# Revit family: DAL_A3-TD06
name_source: partatom
category: Doors
revit_build: Autodesk Revit 2016 (Build: 20150220_1215(x64)
units: mm (PartAtom-declared; Revit-internal decimal feet)

## family parameters
Always vertical = Yes
Cut with Voids When Loaded = No
Host = Wall
Room Calculation Point = No
Shared = No

## types (1)
- TD06 1613 x 2032mm
    Construction Type = TD06
    Description = Purpose Made
    Door Frame = Purpose Made 1,2mm thick pressed metal steel frame with double rebate complete with lugs and base ties as supplied by manufacturer suitable for 115mm wall.
    Door Frame Finish = Red oxide primer factory finish as supplied by manufacturer. Prepare and paint one coat namelcoat zinc chromate metal primer. 1 coat merit universal undercoat and 2 coats gloss enamel paint colour as per finishing schedule.
    Door Panel = Purpose Made Semi-solid Medium Duty flush panel door leaf. 40mm thick with masonite veneer faces suitable for painting and edges to match veneer.
    Door Panel Finish = Stop with polyfilla spackle. Ensure that surfaces to be coated are clean, dry, firm and dust free. Apply 2-3 coats paint as specified.
    Frame Centre = 58 mm
    Function = Interior
    Height = 2064 mm  [stored 6.77165 ft]
    Manufacturer = Duro Pressings (Pty) Ltd.
    Note = All quantities & dimensions to be checked on site by contractor prior to ordering of any material, final quantities to be verified by architect. Schedules to be read in conjunction with latest floor layout drawings & finishing schedules.
    Other = Hinges as supplied by manufacturer. Manufacturer to take note of door weight and to supply hinges accordingly.
    Panel Height = 2032
    Panel Width = 1613
    Wall Closure = By host
    Width = 1677 mm  [stored 5.50197 ft]

note: [stored X ft] marks values corroborated as IEEE doubles in the binary element streams (Revit-internal decimal feet)

## geometry (parser evidence)
native form markers: Sweep x2
no freeform markers — native parametric forms only
